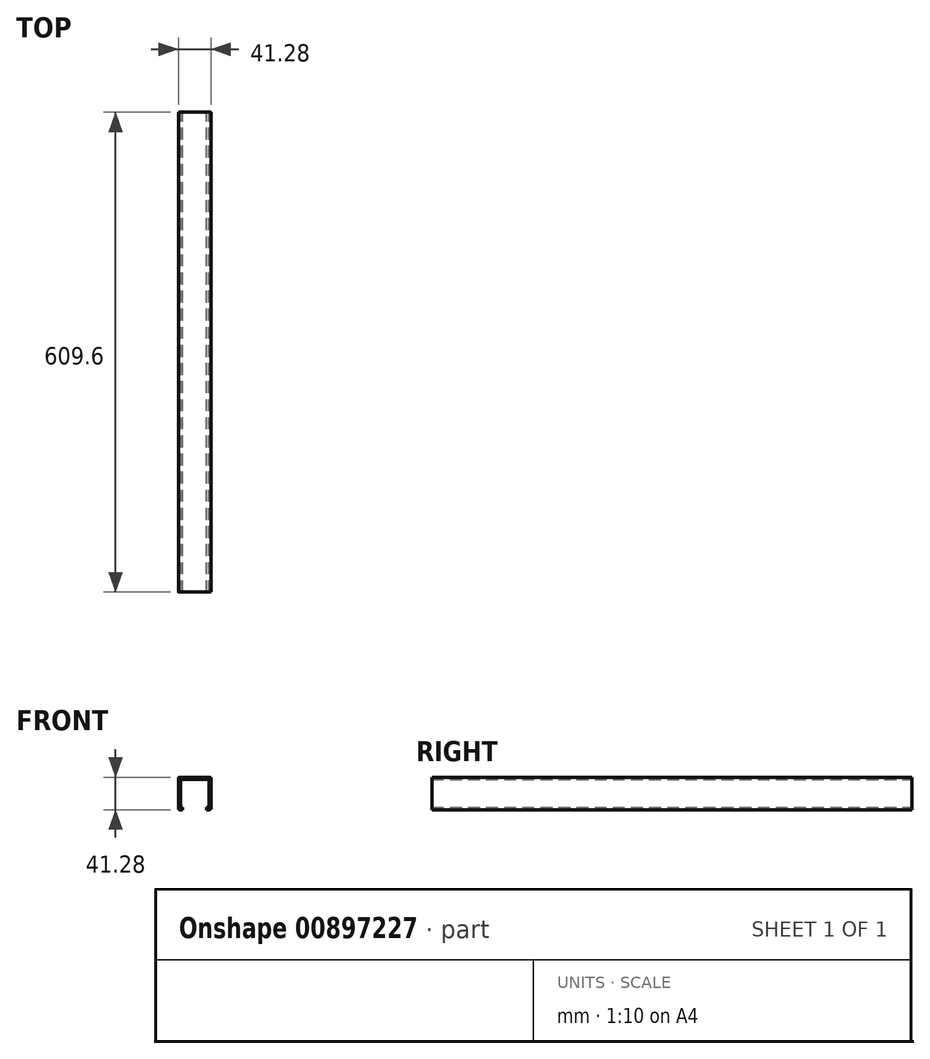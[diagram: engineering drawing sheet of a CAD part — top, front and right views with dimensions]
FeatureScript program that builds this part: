
annotation { "Feature Type Name" : "Feature", "Feature Type Description" : "" }
export const myFeature = defineFeature(function(context is Context, id is Id, definition is map)
    precondition{}
    {
        {
            var Q0;
            Q0=qCreatedBy(makeId("Front.planeOp"),FACE);
            var sketch = newSketch(context, id + "F0", { "sketchPlane" : qUnion([Q0])});
            skLineSegment(sketch, "E0.bottom", {"start": v(19.05, 20.64) * mm, "end": v(-19.05, 20.64) * mm});
            skLineSegment(sketch, "E0.top", {"start": v(19.05, -20.64) * mm, "end": v(15.28, -20.64) * mm});
            skLineSegment(sketch, "E0.left", {"start": v(20.64, 19.05) * mm, "end": v(20.64, -19.05) * mm});
            skLineSegment(sketch, "E0.right", {"start": v(-20.64, 19.05) * mm, "end": v(-20.64, -19.05) * mm});
            skPoint(sketch, "E0.middle", {"position": v(0, 0) * mm});
            skPoint(sketch, "E1.visualSharp", {"position": v(-20.64, 20.64) * mm});
            skArc(sketch, "E1.filletArc", {"start": v(-19.05, 20.64) * mm, "mid": v(-20.17, 20.17) * mm, "end": v(-20.64, 19.05) * mm});
            skPoint(sketch, "E2.visualSharp", {"position": v(20.64, 20.64) * mm});
            skArc(sketch, "E2.filletArc", {"start": v(20.64, 19.05) * mm, "mid": v(20.17, 20.17) * mm, "end": v(19.05, 20.64) * mm});
            skPoint(sketch, "E3.visualSharp", {"position": v(-20.64, -20.64) * mm});
            skArc(sketch, "E3.filletArc", {"start": v(-20.64, -19.05) * mm, "mid": v(-20.17, -20.17) * mm, "end": v(-19.05, -20.64) * mm});
            skPoint(sketch, "E4.visualSharp", {"position": v(20.64, -20.64) * mm});
            skArc(sketch, "E4.filletArc", {"start": v(19.05, -20.64) * mm, "mid": v(20.17, -20.17) * mm, "end": v(20.64, -19.05) * mm});
            skLineSegment(sketch, "E5.bottom", {"start": v(-16.4, 17.98) * mm, "end": v(16.4, 17.98) * mm});
            skLineSegment(sketch, "E5.top", {"start": v(-17.98, -17.98) * mm, "end": v(-15.28, -17.98) * mm});
            skLineSegment(sketch, "E5.left", {"start": v(-17.98, 16.4) * mm, "end": v(-17.98, -17.98) * mm});
            skLineSegment(sketch, "E5.right", {"start": v(17.98, 16.4) * mm, "end": v(17.98, -17.98) * mm});
            skPoint(sketch, "E6.visualSharp", {"position": v(17.98, 17.98) * mm});
            skArc(sketch, "E6.filletArc", {"start": v(17.98, 16.4) * mm, "mid": v(17.52, 17.52) * mm, "end": v(16.4, 17.98) * mm});
            skPoint(sketch, "E7.visualSharp", {"position": v(-17.98, 17.98) * mm});
            skArc(sketch, "E7.filletArc", {"start": v(-16.4, 17.98) * mm, "mid": v(-17.52, 17.52) * mm, "end": v(-17.98, 16.4) * mm});
            skLineSegment(sketch, "E8.left", {"start": v(15.28, -17.98) * mm, "end": v(15.28, -20.64) * mm});
            skLineSegment(sketch, "E8.right", {"start": v(-15.28, -17.98) * mm, "end": v(-15.28, -20.64) * mm});
            skPoint(sketch, "E8.middle", {"position": v(0, -20.64) * mm});
            skPoint(sketch, "E9.orphan", {"position": v(-15.28, -23.3) * mm});
            skLineSegment(sketch, "E10.trimOffspring", {"start": v(-15.28, -20.64) * mm, "end": v(-19.05, -20.64) * mm});
            skLineSegment(sketch, "E11.trimOffspring", {"start": v(15.28, -17.98) * mm, "end": v(17.98, -17.98) * mm});
            skPoint(sketch, "E12.orphan", {"position": v(15.28, -23.3) * mm});
            skSolve(sketch);
        }
        {
            var Q0;
            Q0=makeQuery(id+"F0.imprint","IMPRINT",FACE,{"disambiguationData":[TD([[makeQuery(id+"F0.imprint","IMPRINT",EDGE,{"derivedFrom":sQuery(id+"F0.wireOp",EDGE,"E0.bottom")}),1.0]])]});
            extrude(context, id + "F1", {"entities" : qUnion([Q0]), "endBound" : BoundingType.SYMMETRIC, "depth" : 609.6 * mm, "offsetDistance" : 25.4 * mm});
        }
    });
